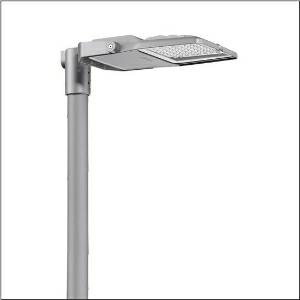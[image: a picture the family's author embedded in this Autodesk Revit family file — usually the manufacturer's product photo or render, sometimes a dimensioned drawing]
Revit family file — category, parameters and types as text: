
# Revit family: floodlight_fl_21_mini___pl61_5xa7775c2c3a_8aba
name_source: partatom
category: Lighting Fixtures
units: mm (PartAtom-declared; Revit-internal decimal feet)

## family parameters
Cut with Voids When Loaded = No
Host = Face
Light Source = No
Part Type = Normal
Room Calculation Point = No
Round Connector Dimension = Use Diameter
Shared = No

## types (1)
- --- (1 x LED, 11960 lm, 89 W, 3000K)
    Apparent Load = 89 VA
    CIE Flux Codes = 33 65 98 100 100
    Color Rendering = 70
    Color Temperature = 3000K
    Default Elevation = 1800 mm
    Description = Floodlight FL 21 mini, floodlight, primary light control with lens, of PMMA, primary optical cover: protective disc, of toughened safety glass, transparent, light distribution: PL61, light emission: direct distribution, installation type: surface-mounted, LED, High Power LED, rated luminous flux: 11.960lm, luminous efficacy: 134lm/W, light colour: 730, colour temperature: 3000K, control gear: ECG Smart Interface, control: flexible luminous flux parameterisation, time-dependent luminous flux control, constant luminous flux control, overheat protection, presetting dimming logarithmic, with terminal, 6-pole, mains connection: 220..240V, AC, 50/60Hz, start of lifetime: 89W, end of lifetime: 94W, reduction: 43W, luminaire housing, of diecast aluminium, powder-coated, Siteco® metallic grey (DB 702S), corrosivity category C5 according to DIN EN ISO 12944, mast bracket, of steel, galvanised, powder-coated, Siteco® metallic grey (DB 702S), protection rating (complete): IP66, insulation class (complete): insulation class II (safety insulation), certification: CE, ENEC, VDE, protection symbol: D, impact resistance: IK08, permissible operating ambient temperature: -40..+40°C, permissible operating ambient temperature for outdoor applications: -40..+50°C, standard: DIN EN 12944, packaging unit: 1 piece

Light Distribution: PL61
    Height = 70 mm
    Lamp = 1 x LED
    Lamp Light Flux = 11960 lm
    Lamp Power = 89 W
    Lamp count = 1
    Length = 485 mm
    Luminous efficacy = 134 lm/W
    Manufacturer = Siteco
    ModVariant = No
    Model = 5XA7775C2C3A
    Number of Poles = 1
    OnlyDefault = Yes
    Power Factor = 1
    Product Name = Floodlight FL 21 mini | PL61
    Product group = floodlight | pylon top
    ProductGroupID = 6101
    Protection Class = Protection class II
    Protection Degree = IP 66
    RLX_Detail_Level = 1
    RlxData = <blob elided: 100701 chars, md5=18cc3f99>
    Socket = socket
    Standby Power = 0 W
    System Light Flux = 11960 lm
    System Power = 89 W
    Type Comments = factory setting: luminous flux: 100 % | dim-lin: 254 | 456 mA
    Type Image = l_1007125.jpg
    URL = http://relux.com
    VarID = @adj_084455
    Voltage = 0 V
    Weight = 0.00 kg
    Width = 337 mm

## geometry (parser evidence)
native form markers: Blend x4, Sweep x11
no freeform markers — native parametric forms only
